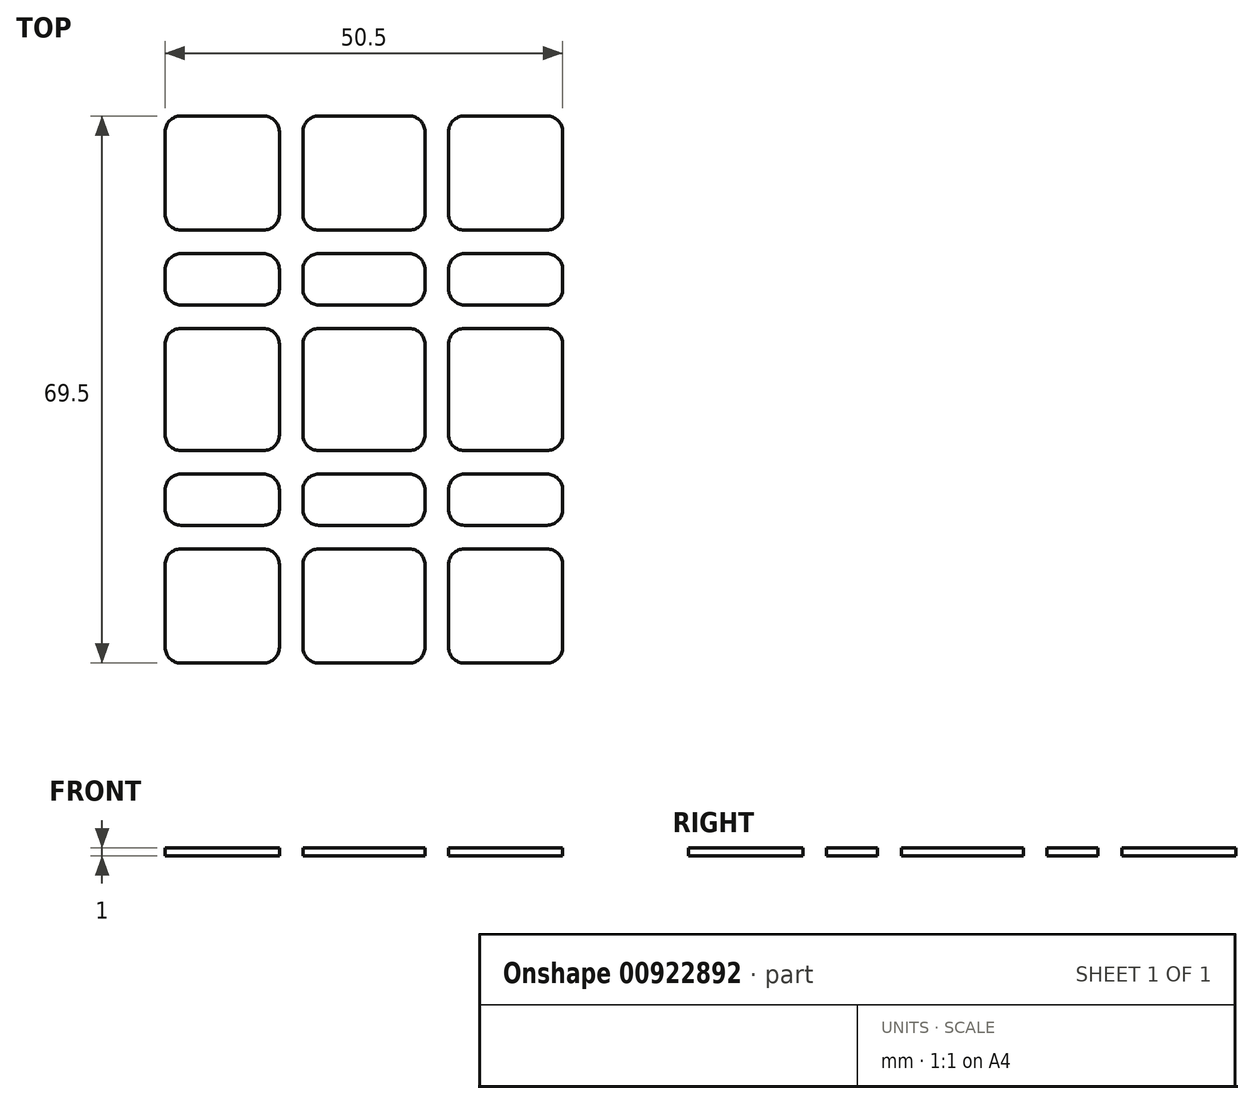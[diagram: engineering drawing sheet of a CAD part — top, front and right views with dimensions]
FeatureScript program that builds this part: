
annotation { "Feature Type Name" : "Feature", "Feature Type Description" : "" }
export const myFeature = defineFeature(function(context is Context, id is Id, definition is map)
    precondition{}
    {
        {
            var Q0;
            Q0=qCreatedBy(makeId("Top.planeOp"),FACE);
            var sketch = newSketch(context, id + "F0", { "sketchPlane" : qUnion([Q0])});
            skLineSegment(sketch, "E0.bottom", {"start": v(27.75, 37.25) * mm, "end": v(-27.75, 37.25) * mm, "construction": true});
            skLineSegment(sketch, "E0.top", {"start": v(27.75, -37.25) * mm, "end": v(-27.75, -37.25) * mm, "construction": true});
            skLineSegment(sketch, "E0.left", {"start": v(27.75, 37.25) * mm, "end": v(27.75, -37.25) * mm, "construction": true});
            skLineSegment(sketch, "E0.right", {"start": v(-27.75, 37.25) * mm, "end": v(-27.75, -37.25) * mm, "construction": true});
            skPoint(sketch, "E0.middle", {"position": v(0, 0) * mm});
            skLineSegment(sketch, "E1", {"start": v(-9.25, 37.25) * mm, "end": v(-9.25, -37.25) * mm, "construction": true});
            skLineSegment(sketch, "E2", {"start": v(9.25, 37.25) * mm, "end": v(9.25, -37.25) * mm, "construction": true});
            skLineSegment(sketch, "E3", {"start": v(-27.75, 0) * mm, "end": v(27.75, 0) * mm, "construction": true});
            skLineSegment(sketch, "E4", {"start": v(-27.75, -9.25) * mm, "end": v(27.75, -9.25) * mm, "construction": true});
            skLineSegment(sketch, "E5", {"start": v(-27.75, -18.75) * mm, "end": v(27.75, -18.75) * mm, "construction": true});
            skLineSegment(sketch, "E6.MirrorCS", {"start": v(-27.75, 9.25) * mm, "end": v(27.75, 9.25) * mm, "construction": true});
            skLineSegment(sketch, "E7.MirrorCS", {"start": v(-27.75, 18.75) * mm, "end": v(27.75, 18.75) * mm, "construction": true});
            skLineSegment(sketch, "E8.bottom", {"start": v(5.75, 7.75) * mm, "end": v(-5.75, 7.75) * mm});
            skLineSegment(sketch, "E8.top", {"start": v(5.75, -7.75) * mm, "end": v(-5.75, -7.75) * mm});
            skLineSegment(sketch, "E8.left", {"start": v(7.75, 5.75) * mm, "end": v(7.75, -5.75) * mm});
            skLineSegment(sketch, "E8.right", {"start": v(-7.75, 5.75) * mm, "end": v(-7.75, -5.75) * mm});
            skLineSegment(sketch, "E9.bottom", {"start": v(-5.75, -10.75) * mm, "end": v(5.75, -10.75) * mm});
            skLineSegment(sketch, "E9.top", {"start": v(-5.75, -17.25) * mm, "end": v(5.75, -17.25) * mm});
            skLineSegment(sketch, "E9.left", {"start": v(-7.75, -12.75) * mm, "end": v(-7.75, -15.25) * mm});
            skLineSegment(sketch, "E9.right", {"start": v(7.75, -12.75) * mm, "end": v(7.75, -15.25) * mm});
            skLineSegment(sketch, "E10.bottom", {"start": v(-12.75, 7.75) * mm, "end": v(-23.25, 7.75) * mm});
            skLineSegment(sketch, "E10.top", {"start": v(-12.75, -7.75) * mm, "end": v(-23.25, -7.75) * mm});
            skLineSegment(sketch, "E10.left", {"start": v(-10.75, 5.75) * mm, "end": v(-10.75, -5.75) * mm});
            skLineSegment(sketch, "E10.right", {"start": v(-25.25, 5.75) * mm, "end": v(-25.25, -5.75) * mm});
            skLineSegment(sketch, "E11.bottom", {"start": v(-23.25, -10.75) * mm, "end": v(-12.75, -10.75) * mm});
            skLineSegment(sketch, "E11.top", {"start": v(-23.25, -17.25) * mm, "end": v(-12.75, -17.25) * mm});
            skLineSegment(sketch, "E11.left", {"start": v(-25.25, -12.75) * mm, "end": v(-25.25, -15.25) * mm});
            skLineSegment(sketch, "E11.right", {"start": v(-10.75, -12.75) * mm, "end": v(-10.75, -15.25) * mm});
            skLineSegment(sketch, "E12.bottom", {"start": v(-23.25, -20.25) * mm, "end": v(-12.75, -20.25) * mm});
            skLineSegment(sketch, "E12.top", {"start": v(-23.25, -34.75) * mm, "end": v(-12.75, -34.75) * mm});
            skLineSegment(sketch, "E12.left", {"start": v(-25.25, -22.25) * mm, "end": v(-25.25, -32.75) * mm});
            skLineSegment(sketch, "E12.right", {"start": v(-10.75, -22.25) * mm, "end": v(-10.75, -32.75) * mm});
            skLineSegment(sketch, "E13.bottom", {"start": v(-5.75, -20.25) * mm, "end": v(5.75, -20.25) * mm});
            skLineSegment(sketch, "E13.top", {"start": v(-5.75, -34.75) * mm, "end": v(5.75, -34.75) * mm});
            skLineSegment(sketch, "E13.left", {"start": v(-7.75, -22.25) * mm, "end": v(-7.75, -32.75) * mm});
            skLineSegment(sketch, "E13.right", {"start": v(7.75, -22.25) * mm, "end": v(7.75, -32.75) * mm});
            skLineSegment(sketch, "E14", {"start": v(0, 0) * mm, "end": v(0, 37.25) * mm, "construction": true});
            skPoint(sketch, "E15.visualSharp", {"position": v(-25.25, 7.75) * mm});
            skArc(sketch, "E15.filletArc", {"start": v(-23.25, 7.75) * mm, "mid": v(-24.66, 7.16) * mm, "end": v(-25.25, 5.75) * mm});
            skPoint(sketch, "E16.visualSharp", {"position": v(-10.75, 7.75) * mm});
            skArc(sketch, "E16.filletArc", {"start": v(-10.75, 5.75) * mm, "mid": v(-11.34, 7.16) * mm, "end": v(-12.75, 7.75) * mm});
            skPoint(sketch, "E17.visualSharp", {"position": v(-7.75, 7.75) * mm});
            skArc(sketch, "E17.filletArc", {"start": v(-5.75, 7.75) * mm, "mid": v(-7.16, 7.16) * mm, "end": v(-7.75, 5.75) * mm});
            skPoint(sketch, "E18.visualSharp", {"position": v(7.75, 7.75) * mm});
            skArc(sketch, "E18.filletArc", {"start": v(7.75, 5.75) * mm, "mid": v(7.16, 7.16) * mm, "end": v(5.75, 7.75) * mm});
            skPoint(sketch, "E19.visualSharp", {"position": v(-25.25, -7.75) * mm});
            skArc(sketch, "E19.filletArc", {"start": v(-25.25, -5.75) * mm, "mid": v(-24.66, -7.16) * mm, "end": v(-23.25, -7.75) * mm});
            skPoint(sketch, "E20.visualSharp", {"position": v(-10.75, -7.75) * mm});
            skArc(sketch, "E20.filletArc", {"start": v(-12.75, -7.75) * mm, "mid": v(-11.34, -7.16) * mm, "end": v(-10.75, -5.75) * mm});
            skPoint(sketch, "E21.visualSharp", {"position": v(-7.75, -7.75) * mm});
            skArc(sketch, "E21.filletArc", {"start": v(-7.75, -5.75) * mm, "mid": v(-7.16, -7.16) * mm, "end": v(-5.75, -7.75) * mm});
            skPoint(sketch, "E22.visualSharp", {"position": v(7.75, -7.75) * mm});
            skArc(sketch, "E22.filletArc", {"start": v(5.75, -7.75) * mm, "mid": v(7.16, -7.16) * mm, "end": v(7.75, -5.75) * mm});
            skPoint(sketch, "E23.visualSharp", {"position": v(7.75, -17.25) * mm});
            skArc(sketch, "E23.filletArc", {"start": v(5.75, -17.25) * mm, "mid": v(7.16, -16.66) * mm, "end": v(7.75, -15.25) * mm});
            skPoint(sketch, "E24.visualSharp", {"position": v(7.75, -10.75) * mm});
            skArc(sketch, "E24.filletArc", {"start": v(7.75, -12.75) * mm, "mid": v(7.16, -11.34) * mm, "end": v(5.75, -10.75) * mm});
            skPoint(sketch, "E25.visualSharp", {"position": v(-7.75, -10.75) * mm});
            skArc(sketch, "E25.filletArc", {"start": v(-5.75, -10.75) * mm, "mid": v(-7.16, -11.34) * mm, "end": v(-7.75, -12.75) * mm});
            skPoint(sketch, "E26.visualSharp", {"position": v(-7.75, -17.25) * mm});
            skArc(sketch, "E26.filletArc", {"start": v(-7.75, -15.25) * mm, "mid": v(-7.16, -16.66) * mm, "end": v(-5.75, -17.25) * mm});
            skPoint(sketch, "E27.visualSharp", {"position": v(-10.75, -17.25) * mm});
            skArc(sketch, "E27.filletArc", {"start": v(-12.75, -17.25) * mm, "mid": v(-11.34, -16.66) * mm, "end": v(-10.75, -15.25) * mm});
            skPoint(sketch, "E28.visualSharp", {"position": v(-10.75, -10.75) * mm});
            skArc(sketch, "E28.filletArc", {"start": v(-10.75, -12.75) * mm, "mid": v(-11.34, -11.34) * mm, "end": v(-12.75, -10.75) * mm});
            skPoint(sketch, "E29.visualSharp", {"position": v(-25.25, -10.75) * mm});
            skArc(sketch, "E29.filletArc", {"start": v(-23.25, -10.75) * mm, "mid": v(-24.66, -11.34) * mm, "end": v(-25.25, -12.75) * mm});
            skPoint(sketch, "E30.visualSharp", {"position": v(-25.25, -17.25) * mm});
            skArc(sketch, "E30.filletArc", {"start": v(-25.25, -15.25) * mm, "mid": v(-24.66, -16.66) * mm, "end": v(-23.25, -17.25) * mm});
            skPoint(sketch, "E31.visualSharp", {"position": v(-25.25, -34.75) * mm});
            skArc(sketch, "E31.filletArc", {"start": v(-25.25, -32.75) * mm, "mid": v(-24.66, -34.16) * mm, "end": v(-23.25, -34.75) * mm});
            skPoint(sketch, "E32.visualSharp", {"position": v(-25.25, -20.25) * mm});
            skArc(sketch, "E32.filletArc", {"start": v(-23.25, -20.25) * mm, "mid": v(-24.66, -20.84) * mm, "end": v(-25.25, -22.25) * mm});
            skPoint(sketch, "E33.visualSharp", {"position": v(-10.75, -20.25) * mm});
            skArc(sketch, "E33.filletArc", {"start": v(-10.75, -22.25) * mm, "mid": v(-11.34, -20.84) * mm, "end": v(-12.75, -20.25) * mm});
            skPoint(sketch, "E34.visualSharp", {"position": v(-10.75, -34.75) * mm});
            skArc(sketch, "E34.filletArc", {"start": v(-12.75, -34.75) * mm, "mid": v(-11.34, -34.16) * mm, "end": v(-10.75, -32.75) * mm});
            skPoint(sketch, "E35.visualSharp", {"position": v(-7.75, -34.75) * mm});
            skArc(sketch, "E35.filletArc", {"start": v(-7.75, -32.75) * mm, "mid": v(-7.16, -34.16) * mm, "end": v(-5.75, -34.75) * mm});
            skPoint(sketch, "E36.visualSharp", {"position": v(-7.75, -20.25) * mm});
            skArc(sketch, "E36.filletArc", {"start": v(-5.75, -20.25) * mm, "mid": v(-7.16, -20.84) * mm, "end": v(-7.75, -22.25) * mm});
            skPoint(sketch, "E37.visualSharp", {"position": v(7.75, -20.25) * mm});
            skArc(sketch, "E37.filletArc", {"start": v(7.75, -22.25) * mm, "mid": v(7.16, -20.84) * mm, "end": v(5.75, -20.25) * mm});
            skPoint(sketch, "E38.visualSharp", {"position": v(7.75, -34.75) * mm});
            skArc(sketch, "E38.filletArc", {"start": v(5.75, -34.75) * mm, "mid": v(7.16, -34.16) * mm, "end": v(7.75, -32.75) * mm});
            skSolve(sketch);
        }
        {
            var Q0;
            Q0=qSketchRegion(id+"F0",true);
            var Q1;
            Q1=qConstructionFilter(qBodyType(qCreatedBy(id+"F0",EDGE),BodyType.WIRE),ConstructionObject.NO);
            extrude(context, id + "F1", {"entities" : qUnion([Q0]), "surfaceEntities" : qUnion([Q1]), "depth" : 1 * mm, "offsetDistance" : 25 * mm});
        }
        {
            var Q0;
            Q0=makeQuery(id+"F1.opExtrude","SWEPT_BODY",BODY,{"disambiguationData":[OSD([sQuery(id+"F0.wireOp",EDGE,"E10.bottom"),sQuery(id+"F0.wireOp",EDGE,"E10.top"),sQuery(id+"F0.wireOp",EDGE,"E10.left"),sQuery(id+"F0.wireOp",EDGE,"E10.right"),sQuery(id+"F0.wireOp",EDGE,"E15.filletArc"),sQuery(id+"F0.wireOp",EDGE,"E16.filletArc"),sQuery(id+"F0.wireOp",EDGE,"E19.filletArc"),sQuery(id+"F0.wireOp",EDGE,"E20.filletArc")])]});
            var Q1;
            Q1=makeQuery(id+"F1.opExtrude","SWEPT_BODY",BODY,{"disambiguationData":[OSD([sQuery(id+"F0.wireOp",EDGE,"E11.bottom"),sQuery(id+"F0.wireOp",EDGE,"E11.top"),sQuery(id+"F0.wireOp",EDGE,"E11.left"),sQuery(id+"F0.wireOp",EDGE,"E11.right"),sQuery(id+"F0.wireOp",EDGE,"E27.filletArc"),sQuery(id+"F0.wireOp",EDGE,"E28.filletArc"),sQuery(id+"F0.wireOp",EDGE,"E29.filletArc"),sQuery(id+"F0.wireOp",EDGE,"E30.filletArc")])]});
            var Q2;
            Q2=makeQuery(id+"F1.opExtrude","SWEPT_BODY",BODY,{"disambiguationData":[OSD([sQuery(id+"F0.wireOp",EDGE,"E12.bottom"),sQuery(id+"F0.wireOp",EDGE,"E12.top"),sQuery(id+"F0.wireOp",EDGE,"E12.left"),sQuery(id+"F0.wireOp",EDGE,"E12.right"),sQuery(id+"F0.wireOp",EDGE,"E31.filletArc"),sQuery(id+"F0.wireOp",EDGE,"E32.filletArc"),sQuery(id+"F0.wireOp",EDGE,"E33.filletArc"),sQuery(id+"F0.wireOp",EDGE,"E34.filletArc")])]});
            var Q3;
            Q3=qCreatedBy(makeId("Right.planeOp"),FACE);
            mirror(context, id + "F2", {"entities" : qUnion([Q0, Q1, Q2]), "mirrorPlane" : qUnion([Q3])});
        }
        {
            var Q0;
            Q0=makeQuery(id+"F1.opExtrude","SWEPT_BODY",BODY,{"disambiguationData":[OSD([sQuery(id+"F0.wireOp",EDGE,"E11.bottom"),sQuery(id+"F0.wireOp",EDGE,"E11.top"),sQuery(id+"F0.wireOp",EDGE,"E11.left"),sQuery(id+"F0.wireOp",EDGE,"E11.right"),sQuery(id+"F0.wireOp",EDGE,"E27.filletArc"),sQuery(id+"F0.wireOp",EDGE,"E28.filletArc"),sQuery(id+"F0.wireOp",EDGE,"E29.filletArc"),sQuery(id+"F0.wireOp",EDGE,"E30.filletArc")])]});
            var Q1;
            Q1=makeQuery(id+"F1.opExtrude","SWEPT_BODY",BODY,{"disambiguationData":[OSD([sQuery(id+"F0.wireOp",EDGE,"E12.bottom"),sQuery(id+"F0.wireOp",EDGE,"E12.top"),sQuery(id+"F0.wireOp",EDGE,"E12.left"),sQuery(id+"F0.wireOp",EDGE,"E12.right"),sQuery(id+"F0.wireOp",EDGE,"E31.filletArc"),sQuery(id+"F0.wireOp",EDGE,"E32.filletArc"),sQuery(id+"F0.wireOp",EDGE,"E33.filletArc"),sQuery(id+"F0.wireOp",EDGE,"E34.filletArc")])]});
            var Q2;
            Q2=makeQuery(id+"F1.opExtrude","SWEPT_BODY",BODY,{"disambiguationData":[OSD([sQuery(id+"F0.wireOp",EDGE,"E13.bottom"),sQuery(id+"F0.wireOp",EDGE,"E13.top"),sQuery(id+"F0.wireOp",EDGE,"E13.left"),sQuery(id+"F0.wireOp",EDGE,"E13.right"),sQuery(id+"F0.wireOp",EDGE,"E35.filletArc"),sQuery(id+"F0.wireOp",EDGE,"E36.filletArc"),sQuery(id+"F0.wireOp",EDGE,"E37.filletArc"),sQuery(id+"F0.wireOp",EDGE,"E38.filletArc")])]});
            var Q3;
            Q3=makeQuery(id+"F1.opExtrude","SWEPT_BODY",BODY,{"disambiguationData":[OSD([sQuery(id+"F0.wireOp",EDGE,"E9.bottom"),sQuery(id+"F0.wireOp",EDGE,"E9.top"),sQuery(id+"F0.wireOp",EDGE,"E9.left"),sQuery(id+"F0.wireOp",EDGE,"E9.right"),sQuery(id+"F0.wireOp",EDGE,"E23.filletArc"),sQuery(id+"F0.wireOp",EDGE,"E24.filletArc"),sQuery(id+"F0.wireOp",EDGE,"E25.filletArc"),sQuery(id+"F0.wireOp",EDGE,"E26.filletArc")])]});
            var Q4;
            Q4=makeQuery(id+"F2.opPattern","COPY",BODY,{"derivedFrom":makeQuery(id+"F1.opExtrude","SWEPT_BODY",BODY,{"disambiguationData":[OSD([sQuery(id+"F0.wireOp",EDGE,"E11.bottom"),sQuery(id+"F0.wireOp",EDGE,"E11.top"),sQuery(id+"F0.wireOp",EDGE,"E11.left"),sQuery(id+"F0.wireOp",EDGE,"E11.right"),sQuery(id+"F0.wireOp",EDGE,"E27.filletArc"),sQuery(id+"F0.wireOp",EDGE,"E28.filletArc"),sQuery(id+"F0.wireOp",EDGE,"E29.filletArc"),sQuery(id+"F0.wireOp",EDGE,"E30.filletArc")])]}),"instanceName":"1"});
            var Q5;
            Q5=makeQuery(id+"F2.opPattern","COPY",BODY,{"derivedFrom":makeQuery(id+"F1.opExtrude","SWEPT_BODY",BODY,{"disambiguationData":[OSD([sQuery(id+"F0.wireOp",EDGE,"E12.bottom"),sQuery(id+"F0.wireOp",EDGE,"E12.top"),sQuery(id+"F0.wireOp",EDGE,"E12.left"),sQuery(id+"F0.wireOp",EDGE,"E12.right"),sQuery(id+"F0.wireOp",EDGE,"E31.filletArc"),sQuery(id+"F0.wireOp",EDGE,"E32.filletArc"),sQuery(id+"F0.wireOp",EDGE,"E33.filletArc"),sQuery(id+"F0.wireOp",EDGE,"E34.filletArc")])]}),"instanceName":"1"});
            var Q6;
            Q6=qCreatedBy(makeId("Front.planeOp"),FACE);
            mirror(context, id + "F3", {"entities" : qUnion([Q0, Q1, Q2, Q3, Q4, Q5]), "mirrorPlane" : qUnion([Q6])});
        }
    });
